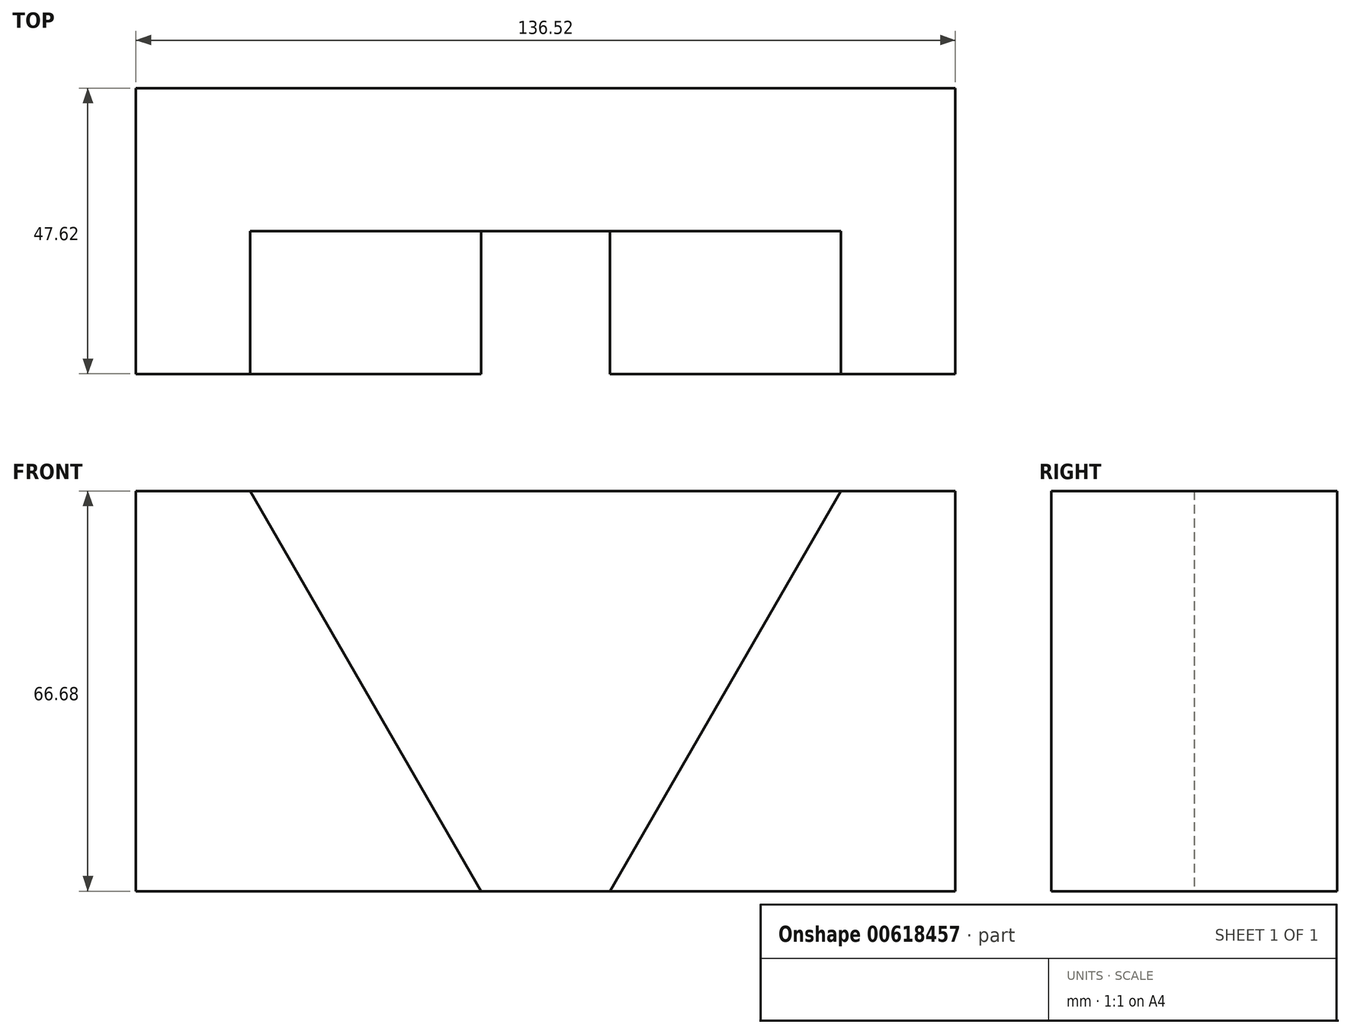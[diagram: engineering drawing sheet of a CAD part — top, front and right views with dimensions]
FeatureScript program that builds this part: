
annotation { "Feature Type Name" : "Feature", "Feature Type Description" : "" }
export const myFeature = defineFeature(function(context is Context, id is Id, definition is map)
    precondition{}
    {
        {
            var Q0;
            Q0=qCreatedBy(makeId("Front.planeOp"),FACE);
            var sketch = newSketch(context, id + "F0", { "sketchPlane" : qUnion([Q0])});
            skLineSegment(sketch, "E0.bottom", {"start": v(-68.26, 33.34) * mm, "end": v(68.26, 33.34) * mm});
            skLineSegment(sketch, "E0.top", {"start": v(-68.26, -33.34) * mm, "end": v(68.26, -33.34) * mm});
            skLineSegment(sketch, "E0.left", {"start": v(-68.26, 33.34) * mm, "end": v(-68.26, -33.34) * mm});
            skLineSegment(sketch, "E0.right", {"start": v(68.26, 33.34) * mm, "end": v(68.26, -33.34) * mm});
            skPoint(sketch, "E0.middle", {"position": v(0, 0) * mm});
            skSolve(sketch);
        }
        {
            var Q0;
            Q0=makeQuery(id+"F0.imprint","IMPRINT",FACE,{"disambiguationData":[TD([[makeQuery(id+"F0.imprint","IMPRINT",EDGE,{"derivedFrom":sQuery(id+"F0.wireOp",EDGE,"E0.bottom")}),-1.0]])]});
            extrude(context, id + "F1", {"entities" : qUnion([Q0]), "depth" : 47.62 * mm, "offsetDistance" : 25.4 * mm});
        }
        {
            var Q0;
            Q0=makeQuery(id+"F1.opExtrude","CAP_FACE",FACE,{"disambiguationData":[OSD([sQuery(id+"F0.wireOp",EDGE,"E0.bottom"),sQuery(id+"F0.wireOp",EDGE,"E0.top"),sQuery(id+"F0.wireOp",EDGE,"E0.left"),sQuery(id+"F0.wireOp",EDGE,"E0.right")])],"isStart":false});
            var sketch = newSketch(context, id + "F2", { "sketchPlane" : qUnion([Q0])});
            skLineSegment(sketch, "E1", {"start": v(-49.21, 33.34) * mm, "end": v(49.21, 33.34) * mm});
            skLineSegment(sketch, "E2", {"start": v(10.72, -33.34) * mm, "end": v(-10.72, -33.34) * mm});
            skLineSegment(sketch, "E3", {"start": v(-49.21, 33.34) * mm, "end": v(-10.72, -33.34) * mm});
            skLineSegment(sketch, "E4", {"start": v(49.21, 33.34) * mm, "end": v(10.72, -33.34) * mm});
            skSolve(sketch);
        }
        {
            var Q0;
            Q0=makeQuery(id+"F2.imprint","IMPRINT",FACE,{"disambiguationData":[TD([[makeQuery(id+"F2.imprint","IMPRINT",EDGE,{"derivedFrom":sQuery(id+"F2.wireOp",EDGE,"E1")}),-1.0]])]});
            extrude(context, id + "F3", {"entities" : qUnion([Q0]), "operationType" : NewBodyOperationType.REMOVE, "oppositeDirection" : true, "depth" : 23.8 * mm, "offsetDistance" : 25.4 * mm});
        }
    });
